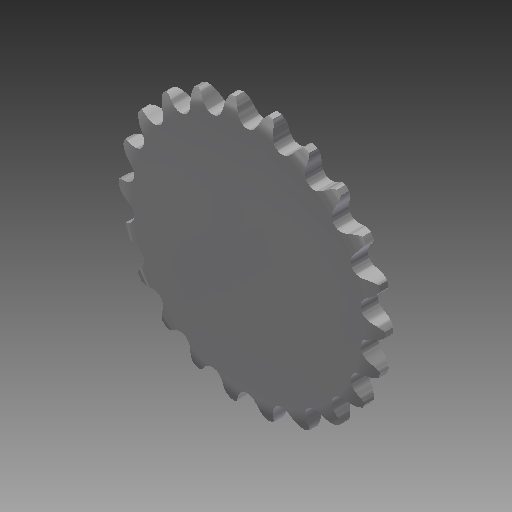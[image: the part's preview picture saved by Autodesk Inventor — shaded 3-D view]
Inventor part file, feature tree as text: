
AUTODESK INVENTOR PART (.ipt)
format: ipt  version: 2017 (Build 210142000, 142)  size: 617,984 bytes
history: native  units: mm
features: other x6, extrude x2, pattern_linear x1, pattern_circular x1
ambient origin geometry x8: Origin, YZ Plane, XZ Plane, XY Plane, X Axis, Y Axis, Z Axis, Center Point
bodies: Solid1 (feature_tree)
feature tree (10):
  other  "Theoretical Tooth Profile"
  other  "Tooth Profile"
  other  "Section Profile"
  other  "Shroud"
  other  "Strand"
  pattern_linear  "Strand Pattern"  Spacing1=44.619381mm  [1 undecoded]
  extrude  "Theoretical Tooth"  Depth=2.855993mm
  extrude  "Tooth"  Depth=1.697355mm
  pattern_circular  "Tooth Pattern"  [2 undecoded]
  other  "Timing Plane"
note: 3 required parameter values undecoded (feature->parameter linkage not recoverable at this tier; creation-order binding heuristic only, values carry confidence <= 0.55)
